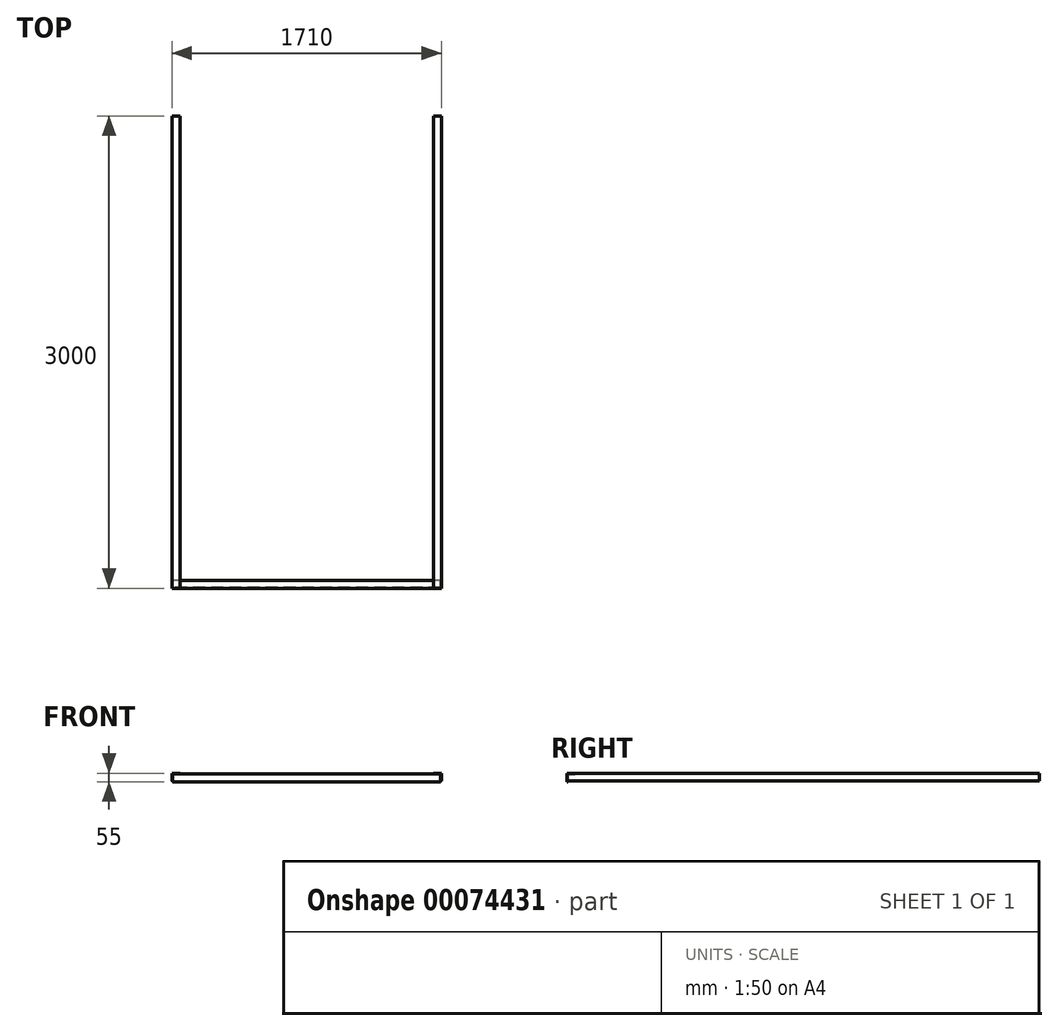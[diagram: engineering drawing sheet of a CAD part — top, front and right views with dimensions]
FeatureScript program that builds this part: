
annotation { "Feature Type Name" : "Feature", "Feature Type Description" : "" }
export const myFeature = defineFeature(function(context is Context, id is Id, definition is map)
    precondition{}
    {
        {
            var Q0;
            Q0=qCreatedBy(makeId("Right.planeOp"),FACE);
            var sketch = newSketch(context, id + "F0", { "sketchPlane" : qUnion([Q0])});
            skLineSegment(sketch, "E0", {"start": v(0, 0) * mm, "end": v(0, 50) * mm});
            skLineSegment(sketch, "E1", {"start": v(0, 50) * mm, "end": v(50, 50) * mm});
            skLineSegment(sketch, "E2", {"start": v(50, 50) * mm, "end": v(50, 45) * mm});
            skLineSegment(sketch, "E3", {"start": v(50, 45) * mm, "end": v(5, 45) * mm});
            skLineSegment(sketch, "E4", {"start": v(5, 45) * mm, "end": v(5, 0) * mm});
            skLineSegment(sketch, "E5", {"start": v(5, 0) * mm, "end": v(0, 0) * mm});
            skSolve(sketch);
        }
        {
            var Q0;
            Q0=makeQuery(id+"F0.imprint","IMPRINT",FACE,{"disambiguationData":[TD([[makeQuery(id+"F0.imprint","IMPRINT",EDGE,{"derivedFrom":sQuery(id+"F0.wireOp",EDGE,"E0")}),-1.0]])]});
            extrude(context, id + "F1", {"entities" : qUnion([Q0]), "depth" : 850 * mm});
        }
        {
            var Q0;
            Q0=makeQuery(id+"F1.opExtrude","CAP_FACE",FACE,{"disambiguationData":[OSD([sQuery(id+"F0.wireOp",EDGE,"E0"),sQuery(id+"F0.wireOp",EDGE,"E1"),sQuery(id+"F0.wireOp",EDGE,"E2"),sQuery(id+"F0.wireOp",EDGE,"E3"),sQuery(id+"F0.wireOp",EDGE,"E4"),sQuery(id+"F0.wireOp",EDGE,"E5")])],"isStart":true});
            extrude(context, id + "F2", {"entities" : qUnion([Q0]), "operationType" : NewBodyOperationType.ADD, "depth" : 850 * mm});
        }
        {
            var Q0;
            {var subQ0=sQuery(id+"F0.wireOp",EDGE,"E0");Q0=makeQuery(id+"F2.boolean.opBoolean","MERGE",FACE,{"derivedFrom":[makeQuery(id+"F1.opExtrude","SWEPT_FACE",FACE,{"disambiguationData":[OSD([subQ0])]}),makeQuery(id+"F2.opExtrude","SWEPT_FACE",FACE,{"disambiguationData":[OSD([subQ0])]})]});}
            var sketch = newSketch(context, id + "F3", { "sketchPlane" : qUnion([Q0])});
            skLineSegment(sketch, "E6", {"start": v(850, 50) * mm, "end": v(850, 5) * mm});
            skLineSegment(sketch, "E7", {"start": v(850, 5) * mm, "end": v(855, 5) * mm});
            skLineSegment(sketch, "E8", {"start": v(855, 5) * mm, "end": v(855, 55) * mm});
            skLineSegment(sketch, "E9", {"start": v(855, 55) * mm, "end": v(805, 55) * mm});
            skLineSegment(sketch, "E10", {"start": v(805, 55) * mm, "end": v(805, 50) * mm});
            skLineSegment(sketch, "E11", {"start": v(805, 50) * mm, "end": v(850, 50) * mm});
            skSolve(sketch);
        }
        {
            var Q0;
            Q0=makeQuery(id+"F3.imprint","IMPRINT",FACE,{"disambiguationData":[TD([[makeQuery(id+"F3.imprint","IMPRINT",EDGE,{"derivedFrom":sQuery(id+"F3.wireOp",EDGE,"E6")}),-1.0]])]});
            extrude(context, id + "F4", {"entities" : qUnion([Q0]), "oppositeDirection" : true, "depth" : 3000 * mm});
        }
        {
            var Q0;
            {var subQ0=sQuery(id+"F0.wireOp",EDGE,"E0");Q0=makeQuery(id+"F2.boolean.opBoolean","MERGE",FACE,{"derivedFrom":[makeQuery(id+"F1.opExtrude","SWEPT_FACE",FACE,{"disambiguationData":[OSD([subQ0])]}),makeQuery(id+"F2.opExtrude","SWEPT_FACE",FACE,{"disambiguationData":[OSD([subQ0])]})]});}
            var sketch = newSketch(context, id + "F5", { "sketchPlane" : qUnion([Q0])});
            skLineSegment(sketch, "E12", {"start": v(-850, 50) * mm, "end": v(-850, 5) * mm});
            skLineSegment(sketch, "E13", {"start": v(-850, 5) * mm, "end": v(-855, 5) * mm});
            skLineSegment(sketch, "E14", {"start": v(-855, 5) * mm, "end": v(-855, 55) * mm});
            skLineSegment(sketch, "E15", {"start": v(-855, 55) * mm, "end": v(-805, 55) * mm});
            skLineSegment(sketch, "E16", {"start": v(-805, 55) * mm, "end": v(-805, 50) * mm});
            skLineSegment(sketch, "E17", {"start": v(-805, 50) * mm, "end": v(-850, 50) * mm});
            skSolve(sketch);
        }
        {
            var Q0;
            Q0=makeQuery(id+"F5.imprint","IMPRINT",FACE,{"disambiguationData":[TD([[makeQuery(id+"F5.imprint","IMPRINT",EDGE,{"derivedFrom":sQuery(id+"F5.wireOp",EDGE,"E12")}),1.0]])]});
            extrude(context, id + "F6", {"entities" : qUnion([Q0]), "oppositeDirection" : true, "depth" : 3000 * mm});
        }
    });
